# Revit family: Toilet_Seat-Round_Closed_Front-KOHLER-PureWarmth-K-10515_1
name_source: partatom
category: Specialty Equipment
units: mm (PartAtom-declared; Revit-internal decimal feet)

## family parameters
Cut with Voids When Loaded = No
Host = Face
OmniClass Number = 23.31.25.00
OmniClass Title = Toilet and Bath Specialties
Part Type = Normal
Room Calculation Point = No
Round Connector Dimension = Use Diameter
Shared = No

## types (3) — shared parameters
ADA Compliant = No
Apparent Load = 144 VA
Assembly Code = C1030200
Date Modified = 08/23/2023
Default Elevation = 15"
Description = Heated Round Front Toilet Seat
Electrical Connector = Yes
Electrical Note = One dedicated circuit required, protected with Class A GroundFault Circuit-Interrupter (GFCI). Outside North America, this device may be known as a Residual Current Device (RCD).
Height = 3"
Length = 18"
Manufacturer = Kohler Co.
Master Format 2014 = 10 28 00
Master Format 2014 Name = Toilet, Bath, and Laundry Accessories
Material = Plastic
Product Documentation Link = https://www.us.kohler.com
Product Name = Purewarmth
Product Page URL = http://www.us.kohler.com
URL = https://www.us.kohler.com
Voltage = 240 V
WaterSense Certified = No
Width = 14 7/8"

## per-type parameters (varying)
| type | Finish | Model | Type |
| 0-White | Kohler-Plastic-0-White | K-10515-0 | 1 |
| 58-Thunder Grey | Kohler-Plastic-58-Thunder_Grey | K-10515-58 | 2 |
| 96-Biscuit | Kohler-Plastic-96-Biscuit | K-10515-96 | 3 |

## geometry (parser evidence)
native form markers: Sweep x7
no freeform markers — native parametric forms only
